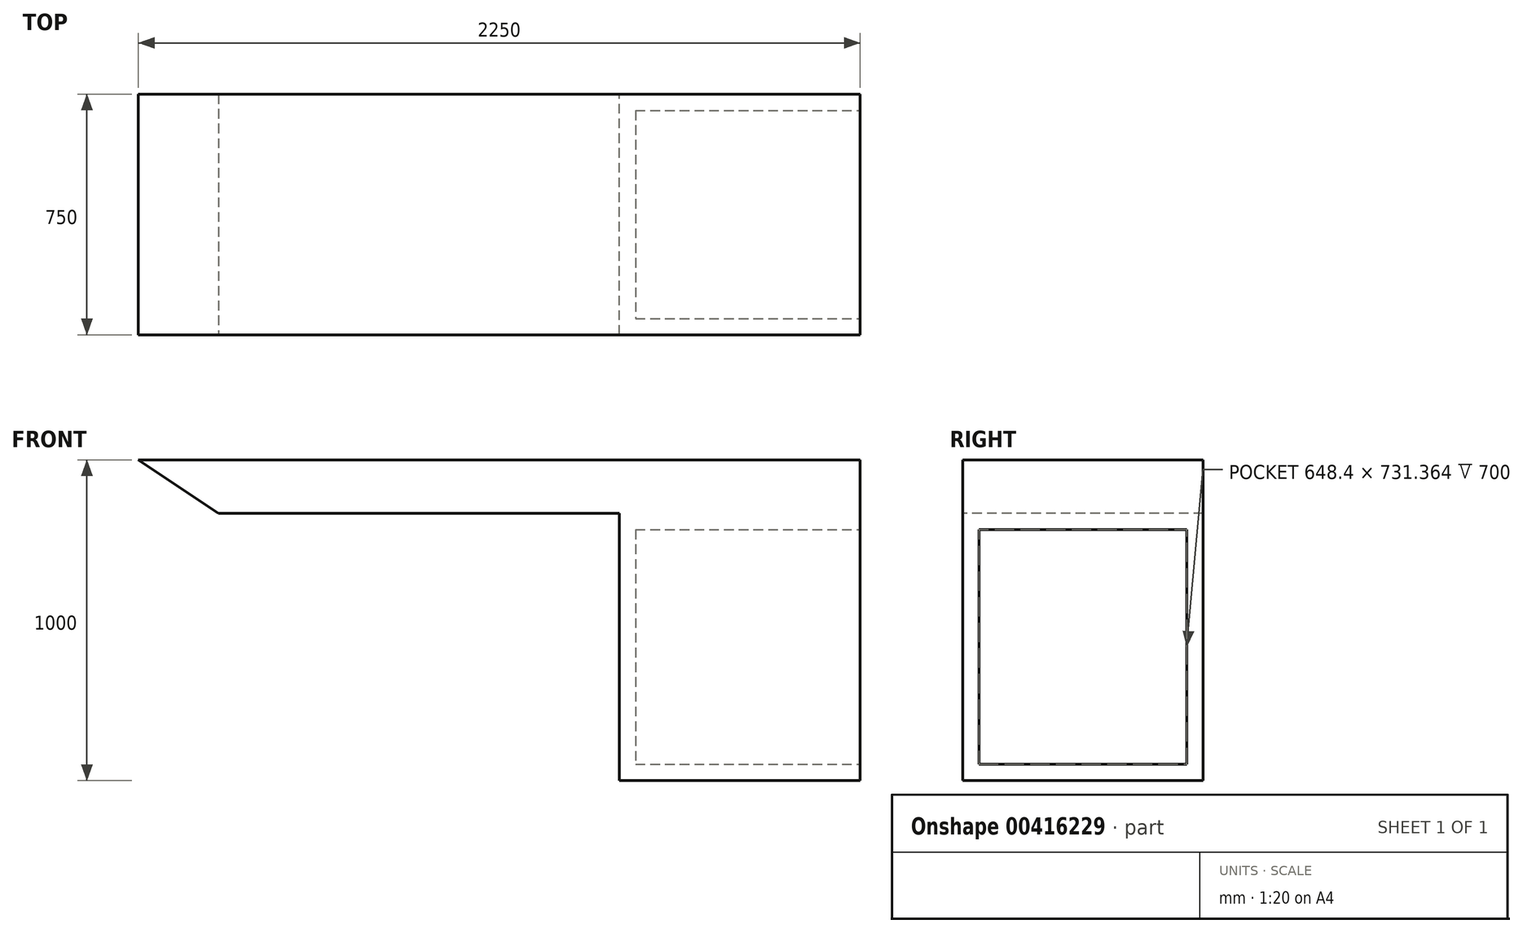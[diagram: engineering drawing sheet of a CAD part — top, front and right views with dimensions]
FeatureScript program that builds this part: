
annotation { "Feature Type Name" : "Feature", "Feature Type Description" : "" }
export const myFeature = defineFeature(function(context is Context, id is Id, definition is map)
    precondition{}
    {
        {
            var Q0;
            Q0=qCreatedBy(makeId("Top.planeOp"),FACE);
            var sketch = newSketch(context, id + "F0", { "sketchPlane" : qUnion([Q0])});
            skLineSegment(sketch, "E0.bottom", {"start": v(-750, -375) * mm, "end": v(750, -375) * mm});
            skLineSegment(sketch, "E0.top", {"start": v(-750, 375) * mm, "end": v(750, 375) * mm});
            skLineSegment(sketch, "E0.left", {"start": v(-750, -375) * mm, "end": v(-750, 375) * mm});
            skLineSegment(sketch, "E0.right", {"start": v(750, -375) * mm, "end": v(750, 375) * mm});
            skPoint(sketch, "E0.middle", {"position": v(0, 0) * mm});
            skSolve(sketch);
        }
        {
            var Q0;
            Q0 = qSketchRegion(id + "F0", true);
            extrude(context, id + "F1", {"entities" : qUnion([Q0]), "oppositeDirection" : true, "depth" : 1000 * mm, "offsetDistance" : 25 * mm});
        }
        {
            var Q0;
            Q0=makeQuery(id+"F1.opExtrude","SWEPT_FACE",FACE,{"disambiguationData":[OSD([sQuery(id+"F0.wireOp",EDGE,"E0.bottom")])]});
            var sketch = newSketch(context, id + "F2", { "sketchPlane" : qUnion([Q0])});
            skLineSegment(sketch, "E1", {"start": v(750, -1000) * mm, "end": v(-750, 0) * mm});
            skLineSegment(sketch, "E2", {"start": v(-750, 0) * mm, "end": v(-750, -1000) * mm});
            skLineSegment(sketch, "E3", {"start": v(-750, -1000) * mm, "end": v(750, -1000) * mm});
            skSolve(sketch);
        }
        {
            var Q0;
            Q0 = qSketchRegion(id + "F2", true);
            extrude(context, id + "F3", {"entities" : qUnion([Q0]), "operationType" : NewBodyOperationType.REMOVE, "oppositeDirection" : true, "depth" : 750 * mm, "offsetDistance" : 25 * mm});
        }
        {
            var Q0;
            Q0=makeQuery(id+"F1.opExtrude","SWEPT_FACE",FACE,{"disambiguationData":[OSD([sQuery(id+"F0.wireOp",EDGE,"E0.right")])]});
            extrude(context, id + "F4", {"entities" : qUnion([Q0]), "operationType" : NewBodyOperationType.ADD, "depth" : 750 * mm, "offsetDistance" : 25 * mm});
        }
        {
            var Q0;
            {var subQ0=sQuery(id+"F0.wireOp",EDGE,"E0.bottom");Q0=makeQuery(id+"F4.boolean.opBoolean","MERGE",FACE,{"derivedFrom":[makeQuery(id+"F1.opExtrude","SWEPT_FACE",FACE,{"disambiguationData":[OSD([subQ0])]}),makeQuery(id+"F4.opExtrude","SWEPT_FACE",FACE,{"disambiguationData":[OSD([subQ0,sQuery(id+"F0.wireOp",EDGE,"E0.right")])]})]});}
            var sketch = newSketch(context, id + "F5", { "sketchPlane" : qUnion([Q0])});
            skLineSegment(sketch, "E4.bottom", {"start": v(-500.38, -166.41) * mm, "end": v(750, -166.41) * mm});
            skLineSegment(sketch, "E4.top", {"start": v(-500.38, -1000) * mm, "end": v(750, -1000) * mm});
            skLineSegment(sketch, "E4.left", {"start": v(-500.38, -166.41) * mm, "end": v(-500.38, -1000) * mm});
            skLineSegment(sketch, "E4.right", {"start": v(750, -166.41) * mm, "end": v(750, -1000) * mm});
            skSolve(sketch);
        }
        {
            var Q0;
            {var subQ0=sQuery(id+"F5.wireOp",EDGE,"E4.bottom");Q0=makeQuery(id+"F5.imprint","IMPRINT",FACE,{"disambiguationData":[TD([[makeQuery(id+"F5.imprint","IMPRINT",EDGE,{"derivedFrom":subQ0}),-1.0]])]});}
            var Q1;
            {var subQ0=sQuery(id+"F5.wireOp",EDGE,"E4.top");Q1=makeQuery(id+"F5.imprint","IMPRINT",FACE,{"disambiguationData":[TD([[makeQuery(id+"F5.imprint","IMPRINT",EDGE,{"derivedFrom":subQ0}),1.0]])]});}
            extrude(context, id + "F6", {"entities" : qUnion([Q0, Q1]), "operationType" : NewBodyOperationType.REMOVE, "oppositeDirection" : true, "depth" : 750 * mm, "offsetDistance" : 25 * mm});
        }
        {
            var Q0;
            Q0=makeQuery(id+"F4.opExtrude","CAP_FACE",FACE,{"disambiguationData":[OSD([sQuery(id+"F0.wireOp",EDGE,"E0.right")])],"isStart":false});
            var sketch = newSketch(context, id + "F7", { "sketchPlane" : qUnion([Q0])});
            skLineSegment(sketch, "E5", {"start": v(-375, -167.04) * mm, "end": v(375, -167.04) * mm});
            skSolve(sketch);
        }
        {
            var Q0;
            {var subQ0=sQuery(id+"F7.wireOp",EDGE,"E5");Q0=makeQuery(id+"F7.imprint","IMPRINT",FACE,{"disambiguationData":[TD([[makeQuery(id+"F7.imprint","IMPRINT",EDGE,{"derivedFrom":subQ0}),-1.0]])]});}
            var sketch = newSketch(context, id + "F8", { "sketchPlane" : qUnion([Q0])});
            skLineSegment(sketch, "E6.bottom", {"start": v(324.2, -217.84) * mm, "end": v(-324.2, -217.84) * mm});
            skLineSegment(sketch, "E6.top", {"start": v(324.2, -949.2) * mm, "end": v(-324.2, -949.2) * mm});
            skLineSegment(sketch, "E6.left", {"start": v(324.2, -217.84) * mm, "end": v(324.2, -949.2) * mm});
            skLineSegment(sketch, "E6.right", {"start": v(-324.2, -217.84) * mm, "end": v(-324.2, -949.2) * mm});
            skPoint(sketch, "E6.middle", {"position": v(0, -583.52) * mm});
            skSolve(sketch);
        }
        {
            var Q0;
            Q0=makeQuery(id+"F8.imprint","IMPRINT",FACE,{"disambiguationData":[TD([[makeQuery(id+"F8.imprint","IMPRINT",EDGE,{"derivedFrom":sQuery(id+"F8.wireOp",EDGE,"E6.bottom")}),1.0]])]});
            extrude(context, id + "F9", {"entities" : qUnion([Q0]), "operationType" : NewBodyOperationType.REMOVE, "oppositeDirection" : true, "depth" : 700 * mm, "offsetDistance" : 25 * mm});
        }
    });
